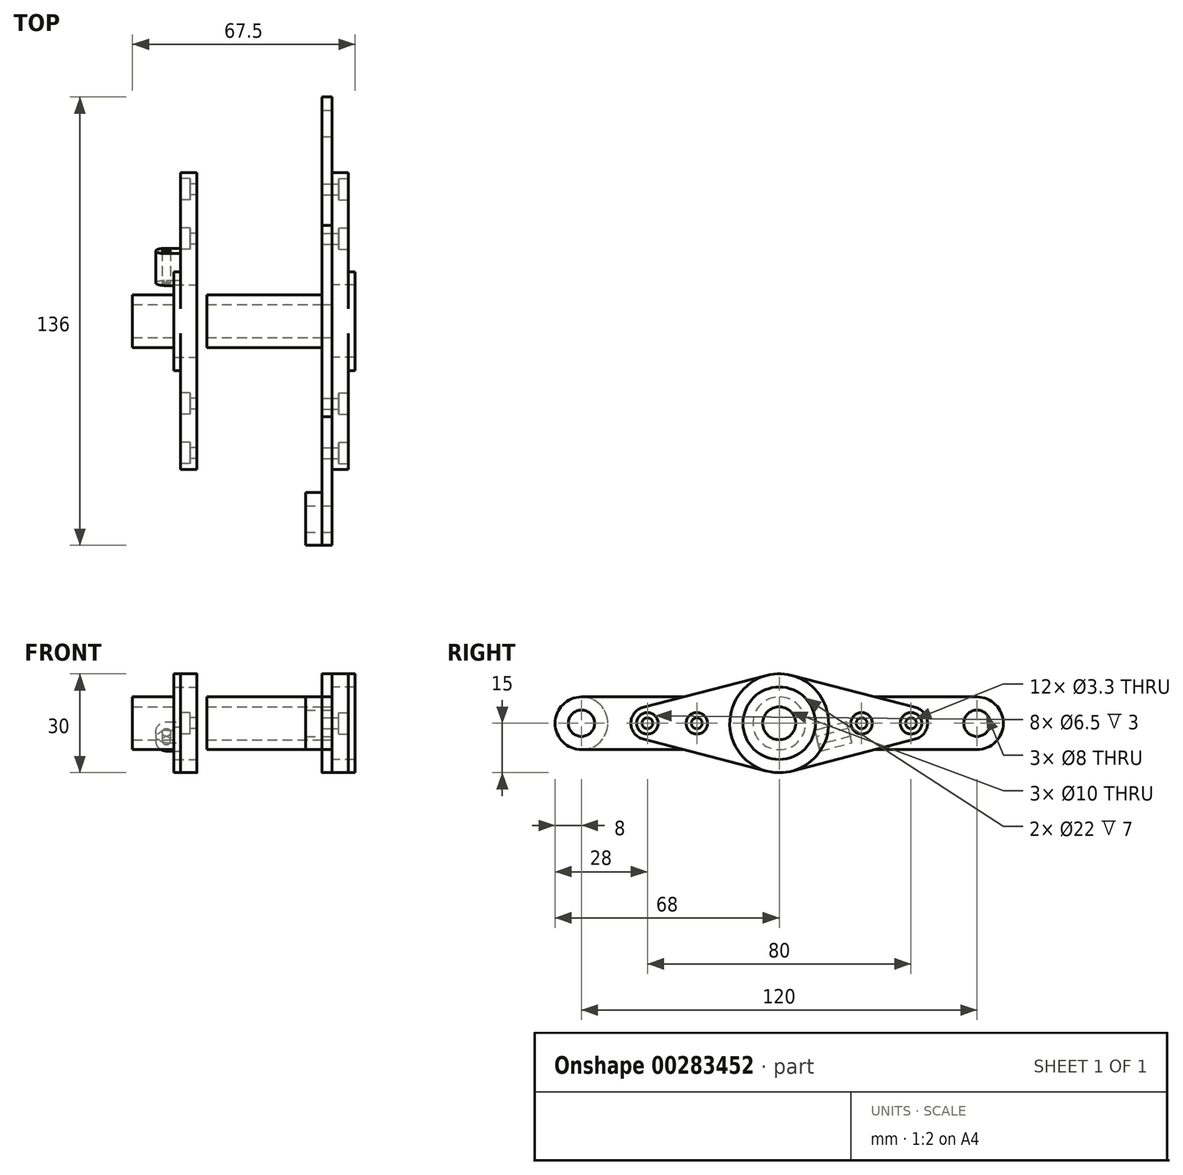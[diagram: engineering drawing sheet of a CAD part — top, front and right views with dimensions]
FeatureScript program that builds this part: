
annotation { "Feature Type Name" : "Feature", "Feature Type Description" : "" }
export const myFeature = defineFeature(function(context is Context, id is Id, definition is map)
    precondition{}
    {
        {
            var Q0;
            Q0=qCreatedBy(makeId("Right.planeOp"),FACE);
            var sketch = newSketch(context, id + "F0", { "sketchPlane" : qUnion([Q0])});
            skCircle(sketch, "E0", {"center": v(0, 0) * mm, "radius": 15 * mm});
            skCircle(sketch, "E1", {"center": v(0, 0) * mm, "radius": 11 * mm});
            skLineSegment(sketch, "E2", {"start": v(41.25, 4.84) * mm, "end": v(3.75, 14.52) * mm});
            skLineSegment(sketch, "E3", {"start": v(41.25, -4.84) * mm, "end": v(3.75, -14.52) * mm});
            skArc(sketch, "E4", {"start": v(41.25, -4.84) * mm, "mid": v(45, 0) * mm, "end": v(41.25, 4.84) * mm});
            skPoint(sketch, "E5.orphan", {"position": v(60, 0) * mm});
            skArc(sketch, "E6", {"start": v(-41.25, 4.84) * mm, "mid": v(-45, 0) * mm, "end": v(-41.25, -4.84) * mm});
            skLineSegment(sketch, "E7", {"start": v(-41.25, 4.84) * mm, "end": v(-3.75, 14.52) * mm});
            skLineSegment(sketch, "E8", {"start": v(-41.25, -4.84) * mm, "end": v(-3.75, -14.52) * mm});
            skPoint(sketch, "E9", {"position": v(-27.5, 0) * mm});
            skPoint(sketch, "E10", {"position": v(27.5, 0) * mm});
            skLineSegment(sketch, "E11", {"start": v(-40, 0) * mm, "end": v(-15, 0) * mm, "construction": true});
            skLineSegment(sketch, "E12", {"start": v(40, 0) * mm, "end": v(15, 0) * mm, "construction": true});
            skSolve(sketch);
        }
        {
            var Q0;
            Q0=makeQuery(id+"F0.imprint","IMPRINT",FACE,{"disambiguationData":[TD([[makeQuery(id+"F0.imprint","IMPRINT",EDGE,{"derivedFrom":sQuery(id+"F0.wireOp",EDGE,"E1")}),-1.0]])]});
            extrude(context, id + "F1", {"entities" : qUnion([Q0]), "depth" : 7 * mm});
        }
        {
            var Q0;
            Q0=makeQuery(id+"F0.imprint","IMPRINT",FACE,{"disambiguationData":[TD([[makeQuery(id+"F0.imprint","IMPRINT",EDGE,{"derivedFrom":sQuery(id+"F0.wireOp",EDGE,"E6")}),1.0]])]});
            var Q1;
            {var subQ0=sQuery(id+"F0.wireOp",EDGE,"E2");Q1=makeQuery(id+"F0.imprint","IMPRINT",FACE,{"disambiguationData":[TD([[makeQuery(id+"F0.imprint","IMPRINT",EDGE,{"derivedFrom":subQ0}),1.0]])]});}
            extrude(context, id + "F2", {"entities" : qUnion([Q0, Q1]), "operationType" : NewBodyOperationType.ADD, "depth" : 5 * mm});
        }
        {
            var Q0;
            {var subQ0=sQuery(id+"F0.wireOp",EDGE,"E0");Q0=makeQuery(id+"F2.boolean.opBoolean","MERGE",FACE,{"derivedFrom":[makeQuery(id+"F1.opExtrude","CAP_FACE",FACE,{"disambiguationData":[OSD([subQ0,sQuery(id+"F0.wireOp",EDGE,"E1")])],"isStart":true}),makeQuery(id+"F2.opExtrude","CAP_FACE",FACE,{"disambiguationData":[OSD([subQ0,sQuery(id+"F0.wireOp",EDGE,"E6"),sQuery(id+"F0.wireOp",EDGE,"E7"),sQuery(id+"F0.wireOp",EDGE,"E8")])],"isStart":true}),makeQuery(id+"F2.opExtrude","CAP_FACE",FACE,{"disambiguationData":[OSD([subQ0,sQuery(id+"F0.wireOp",EDGE,"E2"),sQuery(id+"F0.wireOp",EDGE,"E3"),sQuery(id+"F0.wireOp",EDGE,"E4")])],"isStart":true})]});}
            var sketch = newSketch(context, id + "F3", { "sketchPlane" : qUnion([Q0])});
            skArc(sketch, "E13", {"start": v(-3.75, -14.52) * mm, "mid": v(0, -15) * mm, "end": v(3.75, -14.52) * mm});
            skLineSegment(sketch, "E14.bottom", {"start": v(60, 8) * mm, "end": v(29.02, 8) * mm});
            skLineSegment(sketch, "E14.top", {"start": v(60, -8) * mm, "end": v(29.02, -8) * mm});
            skLineSegment(sketch, "E15", {"start": v(-29.02, 8) * mm, "end": v(-3.75, 14.52) * mm});
            skLineSegment(sketch, "E16", {"start": v(3.75, 14.52) * mm, "end": v(29.02, 8) * mm});
            skLineSegment(sketch, "E17", {"start": v(-29.02, -8) * mm, "end": v(-3.75, -14.52) * mm});
            skLineSegment(sketch, "E18", {"start": v(3.75, -14.52) * mm, "end": v(29.02, -8) * mm});
            skLineSegment(sketch, "E19.trimOffspring", {"start": v(-29.02, 8) * mm, "end": v(-60, 8) * mm});
            skLineSegment(sketch, "E20.trimOffspring", {"start": v(-29.02, -8) * mm, "end": v(-60, -8) * mm});
            skArc(sketch, "E21.trimOffspring", {"start": v(3.75, 14.52) * mm, "mid": v(0, 15) * mm, "end": v(-3.75, 14.52) * mm});
            skArc(sketch, "E22", {"start": v(-60, 8) * mm, "mid": v(-68, 0) * mm, "end": v(-60, -8) * mm});
            skPoint(sketch, "E22.centerSnap0", {"position": v(-95.26, 0) * mm});
            skArc(sketch, "E23", {"start": v(60, -8) * mm, "mid": v(68, 0) * mm, "end": v(60, 8) * mm});
            skPoint(sketch, "E24.orphan", {"position": v(-95.26, 8) * mm});
            skPoint(sketch, "E25.orphan", {"position": v(-95.26, -8) * mm});
            skPoint(sketch, "E26.orphan", {"position": v(95.26, -8) * mm});
            skPoint(sketch, "E27.orphan", {"position": v(95.26, 8) * mm});
            skCircle(sketch, "E28", {"center": v(-60, 0) * mm, "radius": 4 * mm});
            skCircle(sketch, "E29", {"center": v(60, 0) * mm, "radius": 4 * mm});
            skCircle(sketch, "E30", {"center": v(0, 0) * mm, "radius": 5 * mm});
            skSolve(sketch);
        }
        {
            var Q0;
            Q0 = qSketchRegion(id + "F3", true);
            extrude(context, id + "F4", {"entities" : qUnion([Q0]), "depth" : 3 * mm});
        }
        {
            var Q0;
            Q0=makeQuery(id+"F2.opExtrude","CAP_FACE",FACE,{"disambiguationData":[OSD([sQuery(id+"F0.wireOp",EDGE,"E0"),sQuery(id+"F0.wireOp",EDGE,"E6"),sQuery(id+"F0.wireOp",EDGE,"E7"),sQuery(id+"F0.wireOp",EDGE,"E8")])],"isStart":false});
            var sketch = newSketch(context, id + "F5", { "sketchPlane" : qUnion([Q0])});
            skPoint(sketch, "E31", {"position": v(-40, 0) * mm});
            skPoint(sketch, "E32", {"position": v(40, 0) * mm});
            skLineSegment(sketch, "E33", {"start": v(-40, 0) * mm, "end": v(-15, 0) * mm, "construction": true});
            skLineSegment(sketch, "E34", {"start": v(40, 0) * mm, "end": v(15, 0) * mm, "construction": true});
            skPoint(sketch, "E35", {"position": v(-25, 0) * mm});
            skPoint(sketch, "E36", {"position": v(25, 0) * mm});
            skSolve(sketch);
        }
        {
            var Q0;
            Q0=sQuery(id+"F5.wireOp",VERTEX,"E31");
            var Q1;
            Q1=sQuery(id+"F5.wireOp",VERTEX,"E32");
            var Q2;
            Q2=sQuery(id+"F5.wireOp",VERTEX,"E35");
            var Q3;
            Q3=sQuery(id+"F5.wireOp",VERTEX,"E36");
            var Q4;
            Q4=makeQuery(id+"F1.opExtrude","SWEPT_BODY",BODY,{"disambiguationData":[OSD([sQuery(id+"F0.wireOp",EDGE,"E0"),sQuery(id+"F0.wireOp",EDGE,"E1")])]});
            var Q5;
            Q5=makeQuery(id+"F4.opExtrude","SWEPT_BODY",BODY,{"disambiguationData":[OSD([sQuery(id+"F3.wireOp",EDGE,"E13"),sQuery(id+"F3.wireOp",EDGE,"E14.bottom"),sQuery(id+"F3.wireOp",EDGE,"E14.top"),sQuery(id+"F3.wireOp",EDGE,"E15"),sQuery(id+"F3.wireOp",EDGE,"E16"),sQuery(id+"F3.wireOp",EDGE,"E17"),sQuery(id+"F3.wireOp",EDGE,"E18"),sQuery(id+"F3.wireOp",EDGE,"E19.trimOffspring"),sQuery(id+"F3.wireOp",EDGE,"E20.trimOffspring"),sQuery(id+"F3.wireOp",EDGE,"E21.trimOffspring"),sQuery(id+"F3.wireOp",EDGE,"E22"),sQuery(id+"F3.wireOp",EDGE,"E23"),sQuery(id+"F3.wireOp",EDGE,"E28"),sQuery(id+"F3.wireOp",EDGE,"E29"),sQuery(id+"F3.wireOp",EDGE,"E30")])]});
            hole(context, id + "F6", {"style" : HoleStyle.C_BORE, "endStyle" : HoleEndStyle.BLIND, "standardTappedOrClearance" : lookupTablePath({ "standard" : "ISO", "fit" : "Normal", "size" : "M3", "type" : "Clearance" }), "standardBlindInLast" : lookupTablePath({ "fit" : "Standard", "standard" : "ISO", "size" : "M3", "type" : "Clearance" }), "holeDiameter" : 3.3 * mm, "cBoreDiameter" : 6.5 * mm, "cBoreDepth" : 3 * mm, "holeDepth" : 16 * mm, "tappedDepth" : 12 * mm, "tapClearance" : 3, "locations" : qUnion([Q0, Q1, Q2, Q3]), "scope" : qUnion([Q4, Q5])});
        }
        {
            var Q0;
            Q0=makeQuery(id+"F4.opExtrude","CAP_FACE",FACE,{"disambiguationData":[OSD([sQuery(id+"F3.wireOp",EDGE,"E13"),sQuery(id+"F3.wireOp",EDGE,"E14.bottom"),sQuery(id+"F3.wireOp",EDGE,"E14.top"),sQuery(id+"F3.wireOp",EDGE,"E15"),sQuery(id+"F3.wireOp",EDGE,"E16"),sQuery(id+"F3.wireOp",EDGE,"E17"),sQuery(id+"F3.wireOp",EDGE,"E18"),sQuery(id+"F3.wireOp",EDGE,"E19.trimOffspring"),sQuery(id+"F3.wireOp",EDGE,"E20.trimOffspring"),sQuery(id+"F3.wireOp",EDGE,"E21.trimOffspring"),sQuery(id+"F3.wireOp",EDGE,"E22"),sQuery(id+"F3.wireOp",EDGE,"E23"),sQuery(id+"F3.wireOp",EDGE,"E28"),sQuery(id+"F3.wireOp",EDGE,"E29"),sQuery(id+"F3.wireOp",EDGE,"E30")])],"isStart":false});
            var sketch = newSketch(context, id + "F7", { "sketchPlane" : qUnion([Q0])});
            skCircle(sketch, "E37", {"center": v(0, 0) * mm, "radius": 8 * mm});
            skCircle(sketch, "E38", {"center": v(0, 0) * mm, "radius": 5 * mm});
            skCircle(sketch, "E39", {"center": v(60, 0) * mm, "radius": 4 * mm});
            skCircle(sketch, "E40", {"center": v(60, 0) * mm, "radius": 8 * mm});
            skSolve(sketch);
        }
        {
            var Q0;
            Q0=makeQuery(id+"F7.imprint","IMPRINT",FACE,{"disambiguationData":[TD([[makeQuery(id+"F7.imprint","IMPRINT",EDGE,{"derivedFrom":sQuery(id+"F7.wireOp",EDGE,"E37")}),1.0]])]});
            extrude(context, id + "F8", {"entities" : qUnion([Q0]), "depth" : 35 * mm});
        }
        {
            var Q0;
            Q0=makeQuery(id+"F7.imprint","IMPRINT",FACE,{"disambiguationData":[TD([[makeQuery(id+"F7.imprint","IMPRINT",EDGE,{"derivedFrom":sQuery(id+"F7.wireOp",EDGE,"E39")}),-1.0]])]});
            extrude(context, id + "F9", {"entities" : qUnion([Q0]), "depth" : 5 * mm});
        }
        {
            var Q0;
            Q0=makeQuery(id+"F8.opExtrude","CAP_FACE",FACE,{"disambiguationData":[OSD([sQuery(id+"F7.wireOp",EDGE,"E37"),sQuery(id+"F7.wireOp",EDGE,"E38")])],"isStart":true});
            var Q1;
            Q1=makeQuery(id+"F8.opExtrude","CAP_FACE",FACE,{"disambiguationData":[OSD([sQuery(id+"F7.wireOp",EDGE,"E37"),sQuery(id+"F7.wireOp",EDGE,"E38")])],"isStart":false});
            cPlane(context, id + "F10", {"entities" : qUnion([Q0, Q1]), "cplaneType" : CPlaneType.MID_PLANE, "offset" : 25 * mm, "width" : 150 * mm, "height" : 150 * mm});
        }
        {
            var Q0;
            Q0=makeQuery(id+"F1.opExtrude","SWEPT_BODY",BODY,{"disambiguationData":[OSD([sQuery(id+"F0.wireOp",EDGE,"E0"),sQuery(id+"F0.wireOp",EDGE,"E1")])]});
            var Q1;
            Q1=qCreatedBy(id+"F10.planeOp",FACE);
            mirror(context, id + "F11", {"entities" : qUnion([Q0]), "mirrorPlane" : qUnion([Q1])});
        }
        {
            var Q0;
            Q0=makeQuery(id+"F11.opPattern","COPY",FACE,{"derivedFrom":makeQuery(id+"F2.opExtrude","CAP_FACE",FACE,{"disambiguationData":[OSD([sQuery(id+"F0.wireOp",EDGE,"E0"),sQuery(id+"F0.wireOp",EDGE,"E2"),sQuery(id+"F0.wireOp",EDGE,"E3"),sQuery(id+"F0.wireOp",EDGE,"E4")])],"isStart":false}),"instanceName":"1"});
            var sketch = newSketch(context, id + "F12", { "sketchPlane" : qUnion([Q0])});
            skCircle(sketch, "E41", {"center": v(0, 0) * mm, "radius": 8 * mm, "construction": true});
            skLineSegment(sketch, "E42", {"start": v(-29.7, -0.6) * mm, "end": v(-2, -7.75) * mm, "construction": true});
            skLineSegment(sketch, "E43", {"start": v(-22.1, -5.91) * mm, "end": v(-20.48, 0.38) * mm});
            skLineSegment(sketch, "E44", {"start": v(-20.48, 0.38) * mm, "end": v(-10.8, -2.12) * mm});
            skLineSegment(sketch, "E45", {"start": v(-10.8, -2.12) * mm, "end": v(-12.42, -8.41) * mm});
            skLineSegment(sketch, "E46", {"start": v(-12.42, -8.41) * mm, "end": v(-22.1, -5.91) * mm});
            skSolve(sketch);
        }
        {
            var Q0;
            Q0 = qSketchRegion(id + "F12", true);
            extrude(context, id + "F13", {"entities" : qUnion([Q0]), "operationType" : NewBodyOperationType.ADD, "depth" : 25 * mm});
        }
        {
            var Q0;
            Q0=makeQuery(id+"F13.opExtrude","SWEPT_FACE",FACE,{"disambiguationData":[OSD([sQuery(id+"F12.wireOp",EDGE,"E45")])]});
            var sketch = newSketch(context, id + "F14", { "sketchPlane" : qUnion([Q0])});
            skArc(sketch, "E47", {"start": v(-50.25, -4.75) * mm, "mid": v(-53.5, -8) * mm, "end": v(-50.25, -11.25) * mm});
            skCircle(sketch, "E48", {"center": v(-50.25, -8) * mm, "radius": 1.25 * mm});
            skLineSegment(sketch, "E49.bottom", {"start": v(-79.47, -24.28) * mm, "end": v(-50.25, -24.28) * mm});
            skLineSegment(sketch, "E49.top", {"start": v(-79.47, 5.34) * mm, "end": v(-50.25, 5.34) * mm});
            skLineSegment(sketch, "E49.left", {"start": v(-79.47, -24.28) * mm, "end": v(-79.47, 5.34) * mm});
            skLineSegment(sketch, "E49.right", {"start": v(-50.25, -24.28) * mm, "end": v(-50.25, -11.25) * mm});
            skLineSegment(sketch, "E50.trimOffspring", {"start": v(-50.25, -4.75) * mm, "end": v(-50.25, 5.34) * mm});
            skSolve(sketch);
        }
        {
            var Q0;
            Q0 = qSketchRegion(id + "F14", true);
            extrude(context, id + "F15", {"entities" : qUnion([Q0]), "operationType" : NewBodyOperationType.REMOVE, "oppositeDirection" : true, "depth" : 25 * mm});
        }
        {
            var Q0;
            Q0=makeQuery(id+"F11.opPattern","COPY",FACE,{"derivedFrom":makeQuery(id+"F1.opExtrude","CAP_FACE",FACE,{"disambiguationData":[OSD([sQuery(id+"F0.wireOp",EDGE,"E0"),sQuery(id+"F0.wireOp",EDGE,"E1")])],"isStart":false}),"instanceName":"1"});
            var sketch = newSketch(context, id + "F16", { "sketchPlane" : qUnion([Q0])});
            skCircle(sketch, "E51", {"center": v(0, 0) * mm, "radius": 8 * mm});
            skCircle(sketch, "E52", {"center": v(0, 0) * mm, "radius": 5 * mm});
            skSolve(sketch);
        }
        {
            var Q0;
            Q0 = qSketchRegion(id + "F16", true);
            extrude(context, id + "F17", {"entities" : qUnion([Q0]), "depth" : 12.5 * mm});
        }
    });
